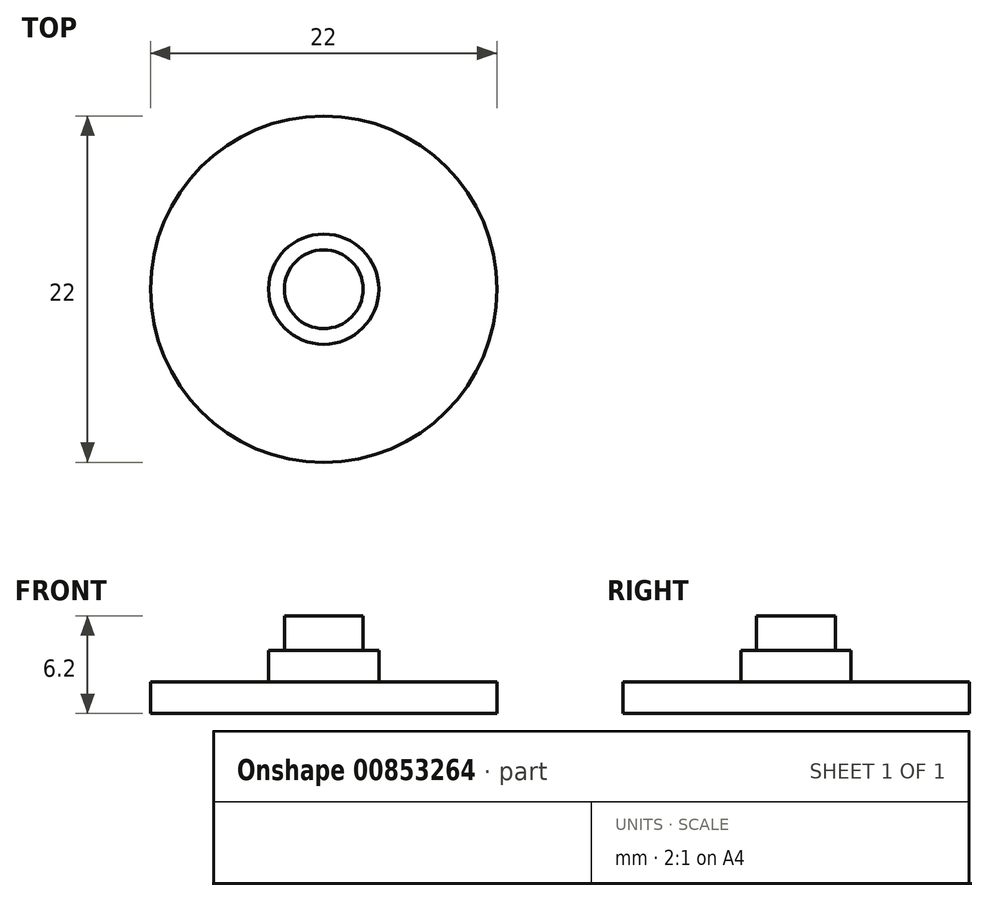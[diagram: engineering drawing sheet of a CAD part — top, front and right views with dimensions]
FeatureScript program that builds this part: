
annotation { "Feature Type Name" : "Feature", "Feature Type Description" : "" }
export const myFeature = defineFeature(function(context is Context, id is Id, definition is map)
    precondition{}
    {
        {
            var Q0;
            Q0=qCreatedBy(makeId("Top.planeOp"),FACE);
            var sketch = newSketch(context, id + "F0", { "sketchPlane" : qUnion([Q0])});
            skCircle(sketch, "E0", {"center": v(0, 0) * mm, "radius": 2.5 * mm});
            skCircle(sketch, "E1", {"center": v(0, 0) * mm, "radius": 3.5 * mm});
            skSolve(sketch);
        }
        {
            var Q0;
            Q0=makeQuery(id+"F0.imprint","IMPRINT",FACE,{"disambiguationData":[TD([[makeQuery(id+"F0.imprint","IMPRINT",EDGE,{"derivedFrom":sQuery(id+"F0.wireOp",EDGE,"E0")}),1.0]])]});
            extrude(context, id + "F1", {"entities" : qUnion([Q0]), "depth" : 2.2 * mm, "offsetDistance" : 25 * mm});
        }
        {
            var Q0;
            Q0=makeQuery(id+"F0.imprint","IMPRINT",FACE,{"disambiguationData":[TD([[makeQuery(id+"F0.imprint","IMPRINT",EDGE,{"derivedFrom":sQuery(id+"F0.wireOp",EDGE,"E0")}),1.0]])]});
            var Q1;
            Q1=makeQuery(id+"F0.imprint","IMPRINT",FACE,{"disambiguationData":[TD([[makeQuery(id+"F0.imprint","IMPRINT",EDGE,{"derivedFrom":sQuery(id+"F0.wireOp",EDGE,"E0")}),-1.0]])]});
            extrude(context, id + "F2", {"entities" : qUnion([Q0, Q1]), "operationType" : NewBodyOperationType.ADD, "oppositeDirection" : true, "depth" : 2 * mm, "offsetDistance" : 25 * mm});
        }
        {
            var Q0;
            Q0=makeQuery(id+"F2.opExtrude","CAP_FACE",FACE,{"disambiguationData":[OSD([sQuery(id+"F0.wireOp",EDGE,"E1")])],"isStart":false});
            var sketch = newSketch(context, id + "F3", { "sketchPlane" : qUnion([Q0])});
            skCircle(sketch, "E2", {"center": v(0, 0) * mm, "radius": 11 * mm});
            skSolve(sketch);
        }
        {
            var Q0;
            Q0=makeQuery(id+"F3.imprint","IMPRINT",FACE,{"disambiguationData":[TD([[makeQuery(id+"F3.imprint","IMPRINT",EDGE,{"derivedFrom":sQuery(id+"F3.wireOp",EDGE,"E2")}),1.0]])]});
            var sketch = newSketch(context, id + "F4", { "sketchPlane" : qUnion([Q0])});
            skSolve(sketch);
        }
        {
            var Q0;
            Q0=makeQuery(id+"F4.imprint","IMPRINT",FACE,{"disambiguationData":[TD([[makeQuery(id+"F4.imprint","IMPRINT",EDGE,{"derivedFrom":makeQuery(id+"F3.imprint","IMPRINT",EDGE,{"derivedFrom":sQuery(id+"F3.wireOp",EDGE,"E2")})}),1.0]])]});
            var sketch = newSketch(context, id + "F5", { "sketchPlane" : qUnion([Q0])});
            skSolve(sketch);
        }
        {
            var Q0;
            Q0=makeQuery(id+"F5.imprint","IMPRINT",FACE,{"disambiguationData":[TD([[makeQuery(id+"F5.imprint","IMPRINT",EDGE,{"derivedFrom":makeQuery(id+"F4.imprint","IMPRINT",EDGE,{"derivedFrom":makeQuery(id+"F3.imprint","IMPRINT",EDGE,{"derivedFrom":sQuery(id+"F3.wireOp",EDGE,"E2")})})}),1.0]])]});
            var Q1;
            Q1=makeQuery(id+"F5.imprint","IMPRINT",FACE,{"disambiguationData":[TD([[makeQuery(id+"F5.imprint","IMPRINT",EDGE,{"derivedFrom":makeQuery(id+"F4.imprint","IMPRINT",EDGE,{"derivedFrom":makeQuery(id+"F3.imprint","IMPRINT",EDGE,{"derivedFrom":makeQuery(id+"F2.opExtrude","CAP_EDGE",EDGE,{"disambiguationData":[OSD([sQuery(id+"F0.wireOp",EDGE,"E1")])],"isStart":false})})})}),-1.0]])]});
            extrude(context, id + "F6", {"entities" : qUnion([Q0, Q1]), "operationType" : NewBodyOperationType.ADD, "depth" : 2 * mm, "offsetDistance" : 25 * mm});
        }
    });
